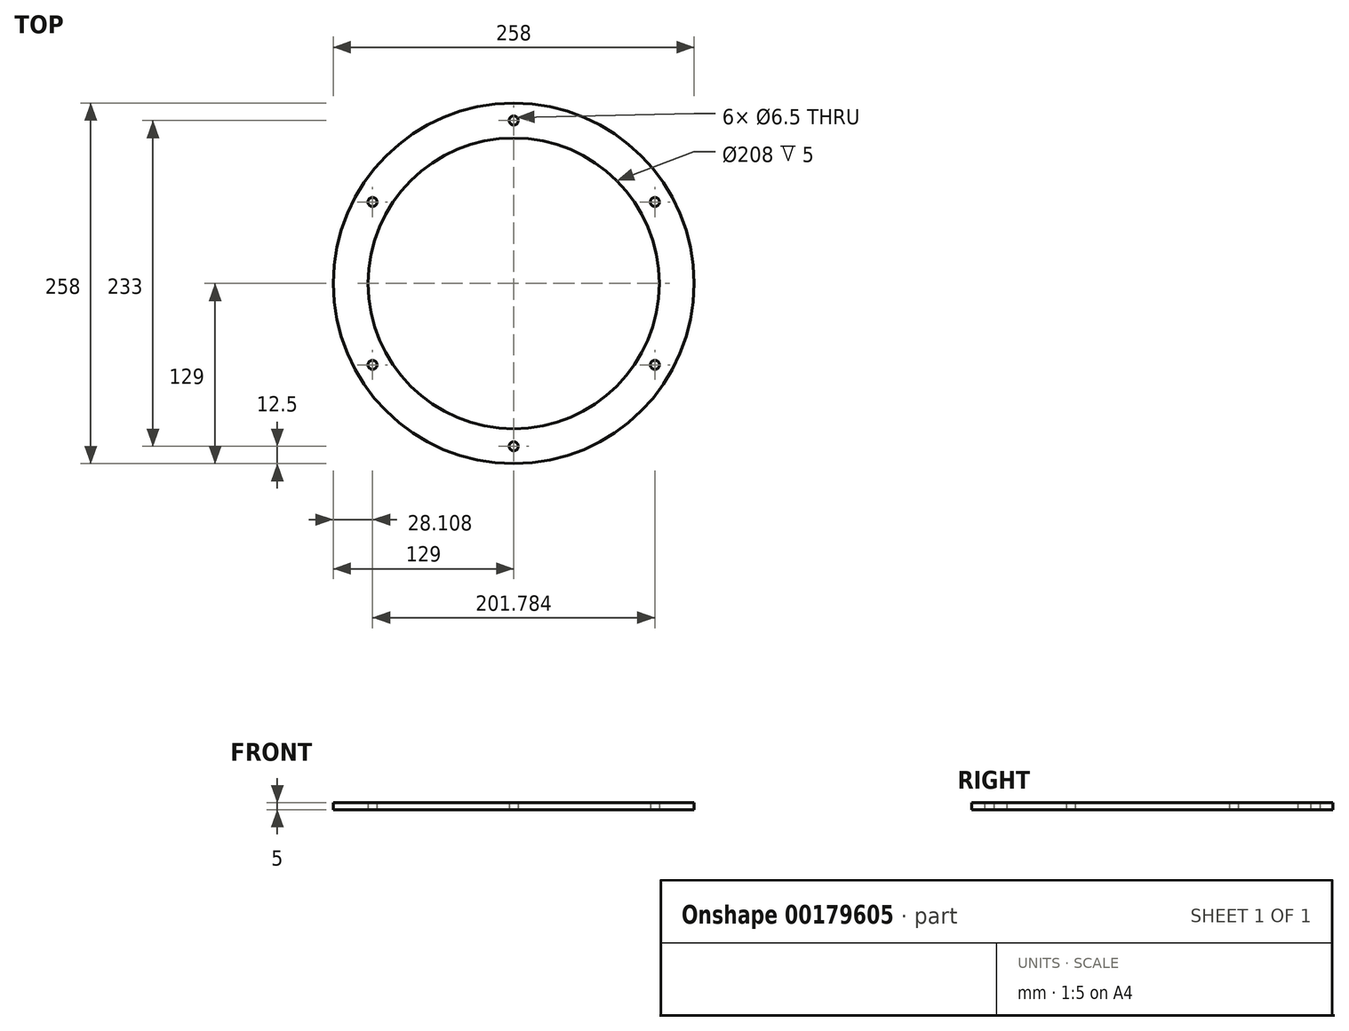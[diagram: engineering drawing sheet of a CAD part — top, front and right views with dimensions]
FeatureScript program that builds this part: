
annotation { "Feature Type Name" : "Feature", "Feature Type Description" : "" }
export const myFeature = defineFeature(function(context is Context, id is Id, definition is map)
    precondition{}
    {
        {
            var Q0;
            Q0=qCreatedBy(makeId("Top.planeOp"),FACE);
            var sketch = newSketch(context, id + "F0", { "sketchPlane" : qUnion([Q0])});
            skCircle(sketch, "E0", {"center": v(0, 0) * mm, "radius": 104 * mm});
            skCircle(sketch, "E1", {"center": v(0, 0) * mm, "radius": 129 * mm});
            skCircle(sketch, "E2", {"center": v(0, 116.5) * mm, "radius": 3.25 * mm});
            skLineSegment(sketch, "E3", {"start": v(0, 104) * mm, "end": v(0, 129) * mm, "construction": true});
            skCircle(sketch, "E4.cCircle", {"center": v(0, 0) * mm, "radius": 116.5 * mm, "construction": true});
            skLineSegment(sketch, "E4.0", {"start": v(0, 116.5) * mm, "end": v(100.9, 58.25) * mm, "construction": true});
            skLineSegment(sketch, "E4.1", {"start": v(100.9, 58.25) * mm, "end": v(100.9, -58.25) * mm, "construction": true});
            skLineSegment(sketch, "E4.2", {"start": v(100.9, -58.25) * mm, "end": v(0, -116.5) * mm, "construction": true});
            skLineSegment(sketch, "E4.3", {"start": v(0, -116.5) * mm, "end": v(-100.9, -58.25) * mm, "construction": true});
            skLineSegment(sketch, "E4.4", {"start": v(-100.9, -58.25) * mm, "end": v(-100.9, 58.25) * mm, "construction": true});
            skLineSegment(sketch, "E4.5", {"start": v(-100.9, 58.25) * mm, "end": v(0, 116.5) * mm, "construction": true});
            skCircle(sketch, "E5", {"center": v(100.9, 58.25) * mm, "radius": 3.25 * mm});
            skCircle(sketch, "E6", {"center": v(100.9, -58.25) * mm, "radius": 3.25 * mm});
            skCircle(sketch, "E7", {"center": v(0, -116.5) * mm, "radius": 3.25 * mm});
            skCircle(sketch, "E8", {"center": v(-100.9, -58.25) * mm, "radius": 3.25 * mm});
            skCircle(sketch, "E9", {"center": v(-100.9, 58.25) * mm, "radius": 3.25 * mm});
            skSolve(sketch);
        }
        {
            var Q0;
            Q0=makeQuery(id+"F0.imprint","IMPRINT",FACE,{"disambiguationData":[TD([[makeQuery(id+"F0.imprint","IMPRINT",EDGE,{"derivedFrom":sQuery(id+"F0.wireOp",EDGE,"E0")}),-1.0]])]});
            extrude(context, id + "F1", {"entities" : qUnion([Q0]), "depth" : 5 * mm});
        }
    });
